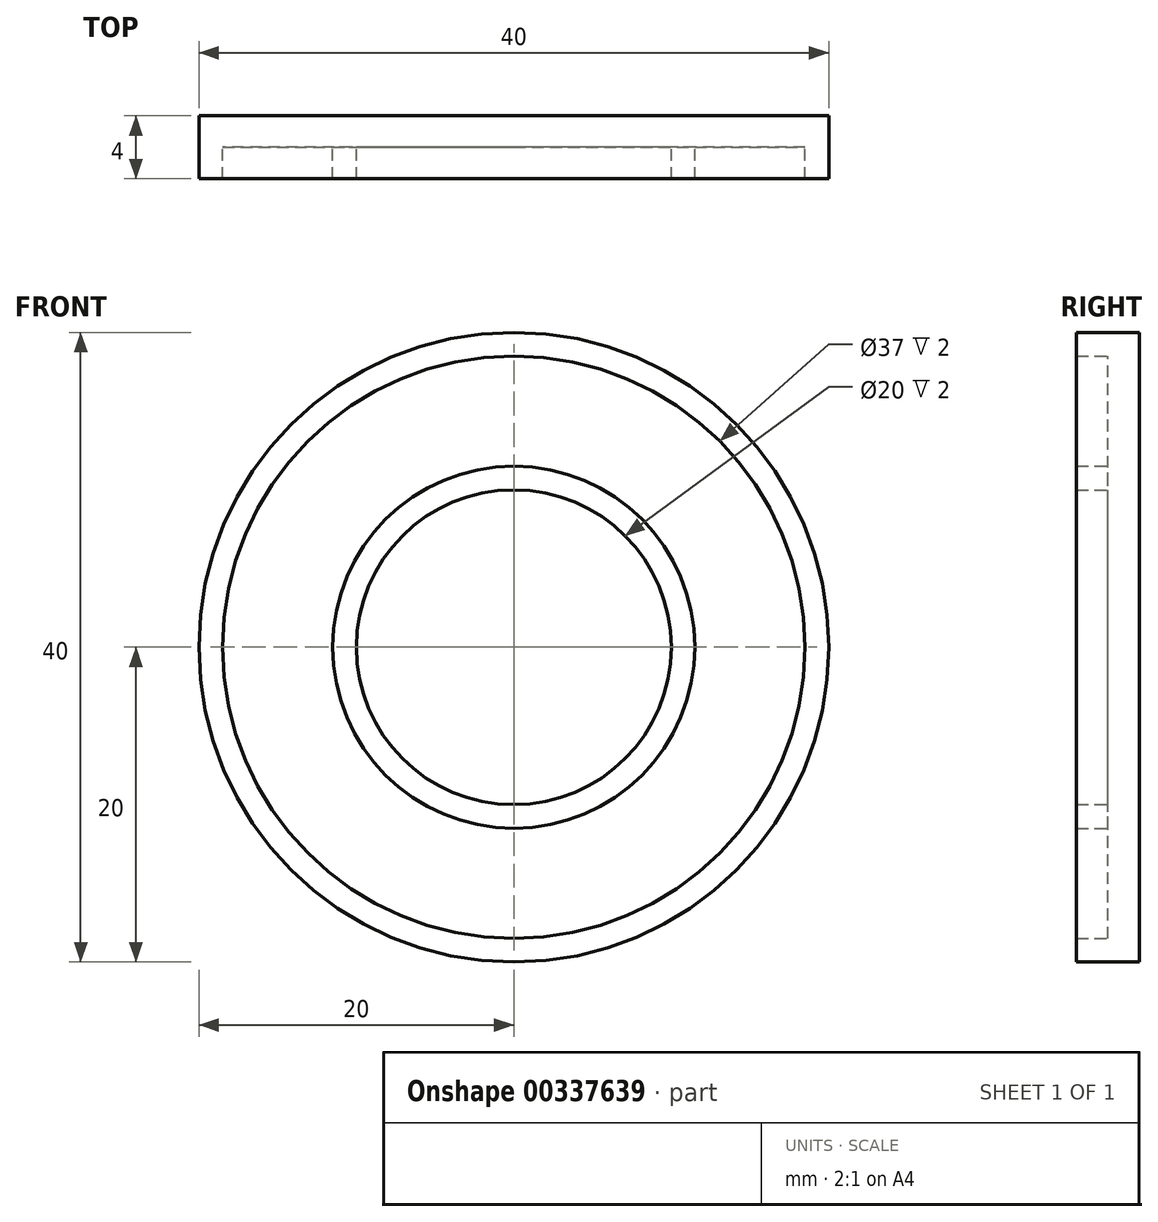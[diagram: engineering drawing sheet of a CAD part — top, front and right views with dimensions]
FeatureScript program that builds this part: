
annotation { "Feature Type Name" : "Feature", "Feature Type Description" : "" }
export const myFeature = defineFeature(function(context is Context, id is Id, definition is map)
    precondition{}
    {
        {
            var Q0;
            Q0=qCreatedBy(makeId("Front.planeOp"),FACE);
            var sketch = newSketch(context, id + "F0", { "sketchPlane" : qUnion([Q0])});
            skCircle(sketch, "E0", {"center": v(0, 0) * mm, "radius": 20 * mm});
            skSolve(sketch);
        }
        {
            var Q0;
            Q0=makeQuery(id+"F0.imprint","IMPRINT",FACE,{"disambiguationData":[TD([[makeQuery(id+"F0.imprint","IMPRINT",EDGE,{"derivedFrom":sQuery(id+"F0.wireOp",EDGE,"E0")}),1.0]])]});
            extrude(context, id + "F1", {"entities" : qUnion([Q0]), "depth" : 2 * mm});
        }
        {
            var Q0;
            Q0=makeQuery(id+"F1.opExtrude","CAP_FACE",FACE,{"disambiguationData":[OSD([sQuery(id+"F0.wireOp",EDGE,"E0")])],"isStart":false});
            var sketch = newSketch(context, id + "F2", { "sketchPlane" : qUnion([Q0])});
            skCircle(sketch, "E1", {"center": v(0, 0) * mm, "radius": 18.5 * mm});
            skSolve(sketch);
        }
        {
            var Q0;
            Q0=makeQuery(id+"F2.imprint","IMPRINT",FACE,{"disambiguationData":[TD([[makeQuery(id+"F2.imprint","IMPRINT",EDGE,{"derivedFrom":sQuery(id+"F2.wireOp",EDGE,"E1")}),-1.0]])]});
            extrude(context, id + "F3", {"entities" : qUnion([Q0]), "operationType" : NewBodyOperationType.ADD, "depth" : 2 * mm});
        }
        {
            var Q0;
            Q0=makeQuery(id+"F1.opExtrude","CAP_FACE",FACE,{"disambiguationData":[OSD([sQuery(id+"F0.wireOp",EDGE,"E0")])],"isStart":false});
            var sketch = newSketch(context, id + "F4", { "sketchPlane" : qUnion([Q0])});
            skCircle(sketch, "E2", {"center": v(0, 0) * mm, "radius": 10 * mm});
            skCircle(sketch, "E3", {"center": v(0, 0) * mm, "radius": 11.5 * mm});
            skSolve(sketch);
        }
        {
            var Q0;
            Q0=makeQuery(id+"F4.imprint","IMPRINT",FACE,{"disambiguationData":[TD([[makeQuery(id+"F4.imprint","IMPRINT",EDGE,{"derivedFrom":sQuery(id+"F4.wireOp",EDGE,"E2")}),-1.0]])]});
            extrude(context, id + "F5", {"entities" : qUnion([Q0]), "operationType" : NewBodyOperationType.ADD, "depth" : 2 * mm});
        }
    });
